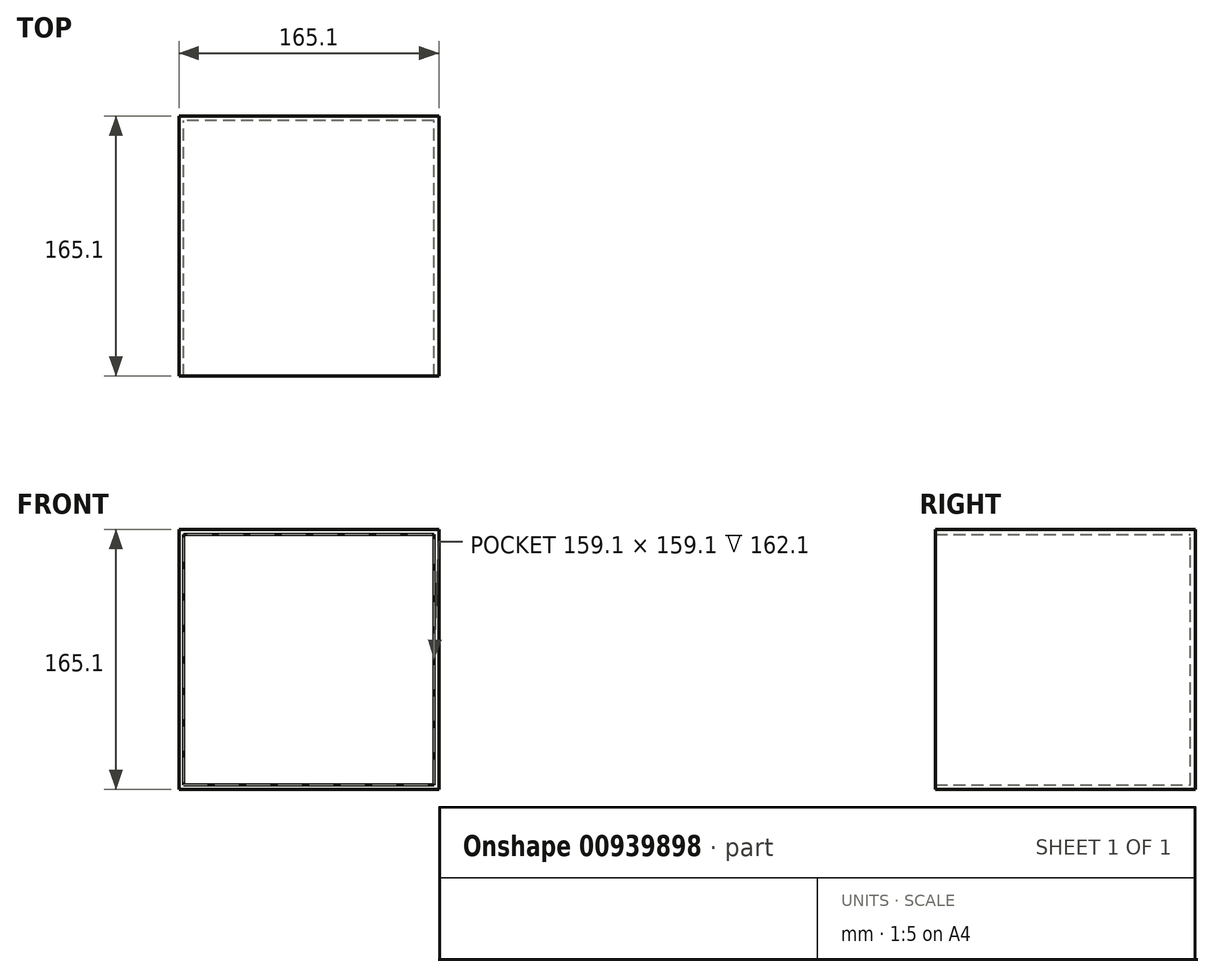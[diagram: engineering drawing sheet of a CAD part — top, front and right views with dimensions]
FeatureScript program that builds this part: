
annotation { "Feature Type Name" : "Feature", "Feature Type Description" : "" }
export const myFeature = defineFeature(function(context is Context, id is Id, definition is map)
    precondition{}
    {
        {
            assignVariable(context, id + "F0", {"name" : "size", "anyValue" : 165.1 * mm});
        }
        {
            var Q0;
            Q0=qCreatedBy(makeId("Front.planeOp"),FACE);
            var sketch = newSketch(context, id + "F1", { "sketchPlane" : qUnion([Q0])});
            skLineSegment(sketch, "E0.bottom", {"start": v(41.45, -147.43) * mm, "end": v(-123.65, -147.43) * mm});
            skLineSegment(sketch, "E0.top", {"start": v(41.45, 17.67) * mm, "end": v(-123.65, 17.67) * mm});
            skLineSegment(sketch, "E0.left", {"start": v(41.45, -147.43) * mm, "end": v(41.45, 17.67) * mm});
            skLineSegment(sketch, "E0.right", {"start": v(-123.65, -147.43) * mm, "end": v(-123.65, 17.67) * mm});
            skSolve(sketch);
        }
        {
            var Q0;
            Q0=qSketchRegion(id+"F1",true);
            extrude(context, id + "F2", {"entities" : qUnion([Q0]), "depth" : getVariable(context, 'size'), "offsetDistance" : 25.4 * mm});
        }
        {
            var Q0;
            Q0=makeQuery(id+"F2.opExtrude","CAP_FACE",FACE,{"disambiguationData":[OSD([sQuery(id+"F1.wireOp",EDGE,"E0.bottom"),sQuery(id+"F1.wireOp",EDGE,"E0.top"),sQuery(id+"F1.wireOp",EDGE,"E0.left"),sQuery(id+"F1.wireOp",EDGE,"E0.right")])],"isStart":false});
            shell(context, id + "F3", {"entities" : qUnion([Q0]), "thickness" : 3 * mm});
        }
    });
